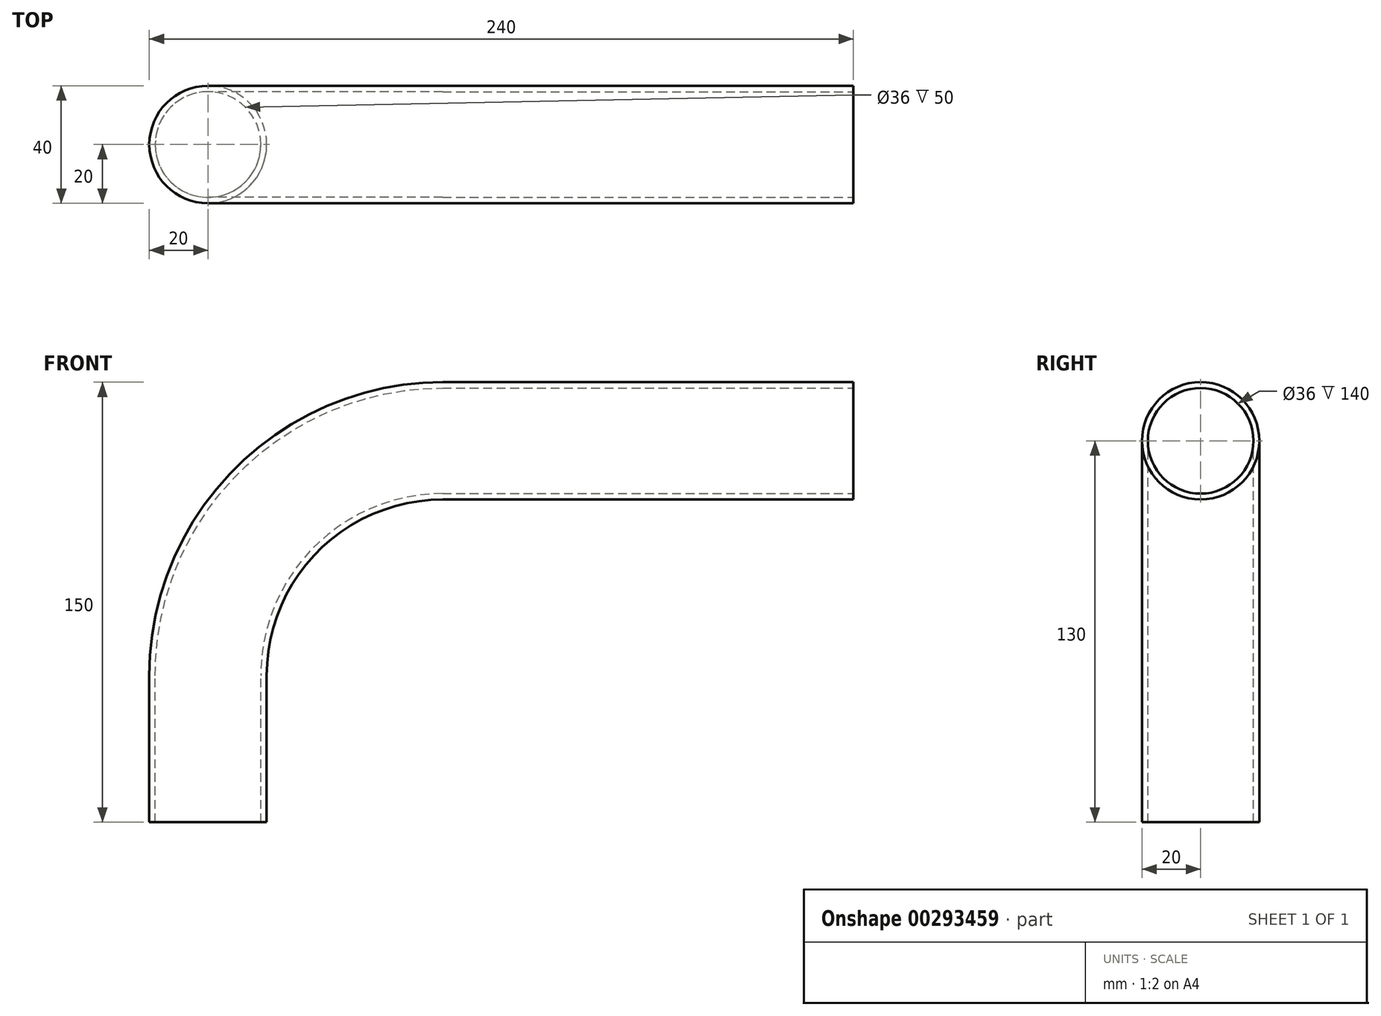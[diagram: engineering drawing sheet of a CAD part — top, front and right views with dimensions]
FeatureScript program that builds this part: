
annotation { "Feature Type Name" : "Feature", "Feature Type Description" : "" }
export const myFeature = defineFeature(function(context is Context, id is Id, definition is map)
    precondition{}
    {
        {
            var Q0;
            Q0=qCreatedBy(makeId("Front.planeOp"),FACE);
            var sketch = newSketch(context, id + "F0", { "sketchPlane" : qUnion([Q0])});
            skLineSegment(sketch, "E0", {"start": v(-160, 0) * mm, "end": v(-160, 50) * mm});
            skArc(sketch, "E1", {"start": v(-160, 50) * mm, "mid": v(-136.57, 106.57) * mm, "end": v(-80, 130) * mm});
            skLineSegment(sketch, "E2", {"start": v(-80, 130) * mm, "end": v(-80, -21.05) * mm, "construction": true});
            skLineSegment(sketch, "E3", {"start": v(9.6, 50) * mm, "end": v(-180.33, 50) * mm, "construction": true});
            skPoint(sketch, "E4.orphan", {"position": v(0, 50) * mm});
            skLineSegment(sketch, "E5", {"start": v(-80, 130) * mm, "end": v(60, 130) * mm});
            skSolve(sketch);
        }
        {
            var Q0;
            Q0=qCreatedBy(makeId("Top.planeOp"),FACE);
            var sketch = newSketch(context, id + "F1", { "sketchPlane" : qUnion([Q0])});
            skCircle(sketch, "E6", {"center": v(-160, 0) * mm, "radius": 20 * mm});
            skSolve(sketch);
        }
        {
            var Q0;
            Q0=makeQuery(id+"F1.imprint","IMPRINT",FACE,{"disambiguationData":[TD([[makeQuery(id+"F1.imprint","IMPRINT",EDGE,{"derivedFrom":sQuery(id+"F1.wireOp",EDGE,"E6")}),1.0]])]});
            var Q1;
            Q1=sQuery(id+"F0.wireOp",EDGE,"E0");
            var Q2;
            Q2=sQuery(id+"F0.wireOp",EDGE,"E1");
            var Q3;
            Q3=sQuery(id+"F0.wireOp",EDGE,"E5");
            sweep(context, id + "F2", {"profiles" : qUnion([Q0]), "path" : qUnion([Q1, Q2, Q3])});
        }
        {
            var Q0;
            Q0=makeQuery(id+"F2.opSweep","CAP_FACE",FACE,{"disambiguationData":[OSD([sQuery(id+"F0.wireOp",VERTEX,"E0.start"),sQuery(id+"F1.wireOp",EDGE,"E6")])],"isStart":true});
            var Q1;
            Q1=makeQuery(id+"F2.opSweep","CAP_FACE",FACE,{"disambiguationData":[OSD([sQuery(id+"F0.wireOp",VERTEX,"E5.end"),sQuery(id+"F1.wireOp",EDGE,"E6")])],"isStart":false});
            shell(context, id + "F3", {"entities" : qUnion([Q0, Q1]), "thickness" : 2 * mm});
        }
    });
